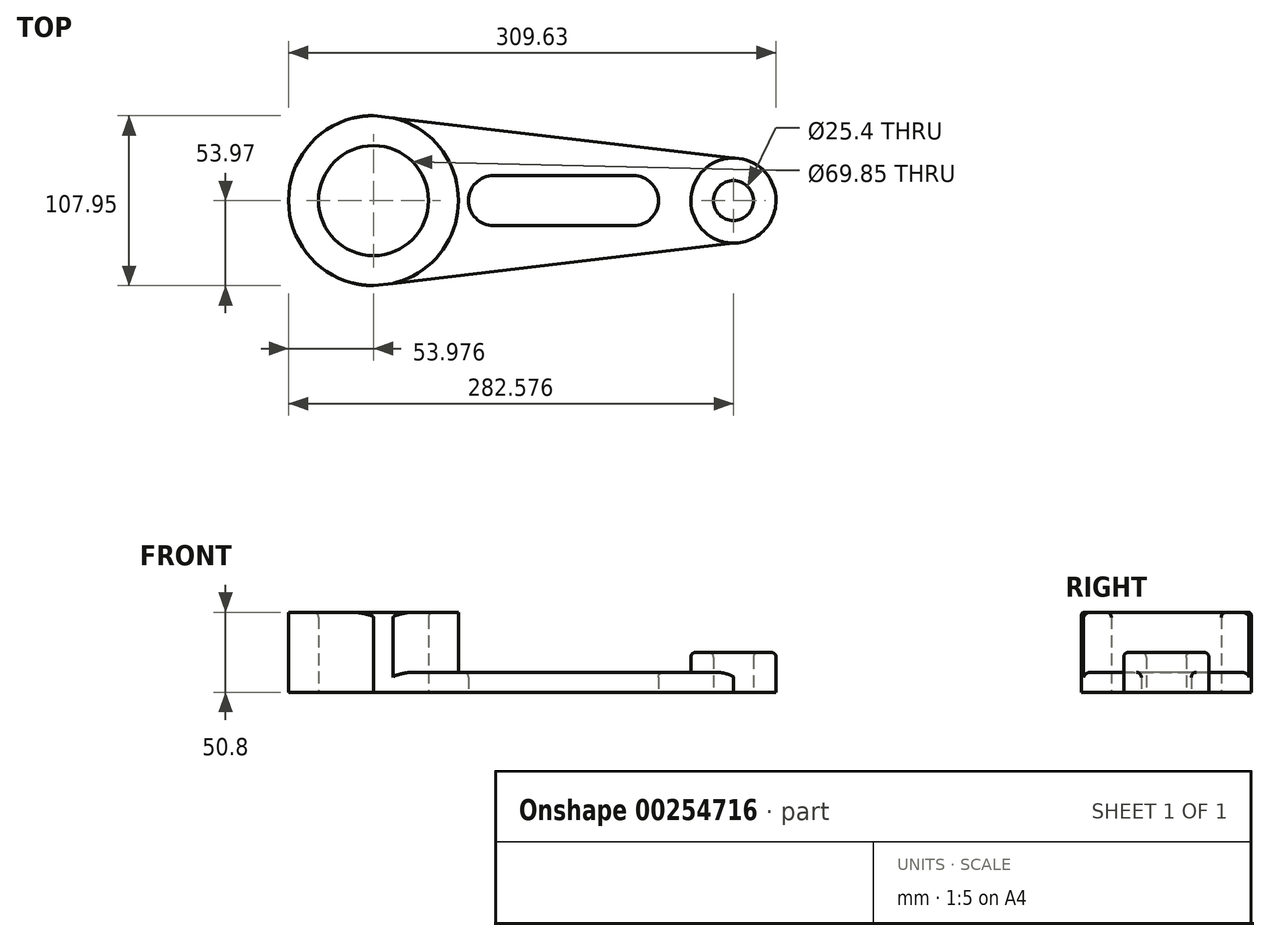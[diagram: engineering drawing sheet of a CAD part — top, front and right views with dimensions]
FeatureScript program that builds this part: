
annotation { "Feature Type Name" : "Feature", "Feature Type Description" : "" }
export const myFeature = defineFeature(function(context is Context, id is Id, definition is map)
    precondition{}
    {
        {
            var Q0;
            Q0=qCreatedBy(makeId("Top.planeOp"),FACE);
            var sketch = newSketch(context, id + "F0", { "sketchPlane" : qUnion([Q0])});
            skCircle(sketch, "E0", {"center": v(-200.57, 15.87) * mm, "radius": 34.93 * mm});
            skCircle(sketch, "E1", {"center": v(-200.57, 15.87) * mm, "radius": 53.98 * mm});
            skCircle(sketch, "E2", {"center": v(28.03, 15.87) * mm, "radius": 12.7 * mm});
            skCircle(sketch, "E3", {"center": v(28.03, 15.87) * mm, "radius": 27.05 * mm});
            skArc(sketch, "E4", {"start": v(-124.37, 31.75) * mm, "mid": v(-140.25, 15.87) * mm, "end": v(-124.37, 0) * mm});
            skArc(sketch, "E5", {"start": v(-35.47, 0) * mm, "mid": v(-19.6, 15.87) * mm, "end": v(-35.47, 31.75) * mm});
            skLineSegment(sketch, "E6", {"start": v(-124.37, 31.75) * mm, "end": v(-35.47, 31.75) * mm});
            skLineSegment(sketch, "E7", {"start": v(-124.37, 0) * mm, "end": v(-35.47, 0) * mm});
            skLineSegment(sketch, "E8", {"start": v(-200.57, 69.85) * mm, "end": v(28.03, 42.92) * mm});
            skLineSegment(sketch, "E9", {"start": v(-200.57, -38.1) * mm, "end": v(28.03, -11.18) * mm});
            skSolve(sketch);
        }
        {
            var Q0;
            Q0=makeQuery(id+"F0.imprint","IMPRINT",FACE,{"disambiguationData":[TD([[makeQuery(id+"F0.imprint","IMPRINT",EDGE,{"derivedFrom":sQuery(id+"F0.wireOp",EDGE,"E4")}),-1.0]])]});
            extrude(context, id + "F1", {"entities" : qUnion([Q0]), "depth" : 12.7 * mm});
        }
        {
            var Q0;
            Q0=makeQuery(id+"F1.opExtrude","CAP_EDGE",EDGE,{"disambiguationData":[OSD([sQuery(id+"F0.wireOp",EDGE,"E9")])],"isStart":false});
            var Q1;
            Q1=makeQuery(id+"F1.opExtrude","CAP_EDGE",EDGE,{"disambiguationData":[OSD([sQuery(id+"F0.wireOp",EDGE,"E8")])],"isStart":false});
            fillet(context, id + "F2", {"entities" : qUnion([Q0, Q1]), "radius" : 3.17 * mm, "tangentPropagation" : true, "allowEdgeOverflow" : false});
        }
        {
            var Q0;
            Q0=makeQuery(id+"F0.imprint","IMPRINT",FACE,{"disambiguationData":[TD([[makeQuery(id+"F0.imprint","IMPRINT",EDGE,{"derivedFrom":sQuery(id+"F0.wireOp",EDGE,"E2")}),-1.0]])]});
            extrude(context, id + "F3", {"entities" : qUnion([Q0]), "operationType" : NewBodyOperationType.ADD, "depth" : 25.4 * mm});
        }
        {
            var Q0;
            Q0=makeQuery(id+"F0.imprint","IMPRINT",FACE,{"disambiguationData":[TD([[makeQuery(id+"F0.imprint","IMPRINT",EDGE,{"derivedFrom":sQuery(id+"F0.wireOp",EDGE,"E0")}),-1.0]])]});
            extrude(context, id + "F4", {"entities" : qUnion([Q0]), "operationType" : NewBodyOperationType.ADD, "depth" : 50.8 * mm});
        }
        {
            var Q0;
            {var subQ0=sQuery(id+"F0.wireOp",EDGE,"E1");Q0=makeQuery(id+"F4.opExtrude","CAP_EDGE",EDGE,{"disambiguationData":[OSD([subQ0]),TDD([makeQuery(id+"F0.imprint","IMPRINT",EDGE,{"disambiguationData":[TD([[makeQuery(id+"F0.imprint","INTERSECT",VERTEX,{"disambiguationData":[OD(0.0)],"derivedFrom":[subQ0,sQuery(id+"F0.wireOp",EDGE,"E8")]}),-1.0]])],"derivedFrom":subQ0})])],"isStart":false});}
            var Q1;
            {var subQ0=sQuery(id+"F0.wireOp",EDGE,"E1");Q1=makeQuery(id+"F4.opExtrude","CAP_EDGE",EDGE,{"disambiguationData":[OSD([subQ0]),TDD([makeQuery(id+"F0.imprint","IMPRINT",EDGE,{"disambiguationData":[TD([[makeQuery(id+"F0.imprint","INTERSECT",VERTEX,{"disambiguationData":[OD(1.0)],"derivedFrom":[subQ0,sQuery(id+"F0.wireOp",EDGE,"E8")]}),1.0]])],"derivedFrom":subQ0})])],"isStart":false});}
            var Q2;
            Q2=makeQuery(id+"F4.opExtrude","CAP_EDGE",EDGE,{"disambiguationData":[OSD([sQuery(id+"F0.wireOp",EDGE,"E9")])],"isStart":false});
            var Q3;
            Q3=makeQuery(id+"F4.opExtrude","CAP_EDGE",EDGE,{"disambiguationData":[OSD([sQuery(id+"F0.wireOp",EDGE,"E8")])],"isStart":false});
            var Q4;
            Q4=makeQuery(id+"F3.opExtrude","CAP_EDGE",EDGE,{"disambiguationData":[OSD([sQuery(id+"F0.wireOp",EDGE,"E3")])],"isStart":false});
            fillet(context, id + "F5", {"entities" : qUnion([Q0, Q1, Q2, Q3, Q4]), "radius" : 3.17 * mm, "tangentPropagation" : true, "allowEdgeOverflow" : false});
        }
        {
            var Q0;
            Q0=makeQuery(id+"F4.opExtrude","CAP_EDGE",EDGE,{"disambiguationData":[OSD([sQuery(id+"F0.wireOp",EDGE,"E0")])],"isStart":false});
            var Q1;
            Q1=makeQuery(id+"F3.opExtrude","CAP_EDGE",EDGE,{"disambiguationData":[OSD([sQuery(id+"F0.wireOp",EDGE,"E2")])],"isStart":false});
            var Q2;
            Q2=makeQuery(id+"F1.opExtrude","CAP_EDGE",EDGE,{"disambiguationData":[OSD([sQuery(id+"F0.wireOp",EDGE,"E7")])],"isStart":false});
            var Q3;
            Q3=makeQuery(id+"F1.opExtrude","CAP_EDGE",EDGE,{"disambiguationData":[OSD([sQuery(id+"F0.wireOp",EDGE,"E4")])],"isStart":false});
            var Q4;
            Q4=makeQuery(id+"F1.opExtrude","CAP_EDGE",EDGE,{"disambiguationData":[OSD([sQuery(id+"F0.wireOp",EDGE,"E5")])],"isStart":false});
            var Q5;
            Q5=makeQuery(id+"F1.opExtrude","CAP_EDGE",EDGE,{"disambiguationData":[OSD([sQuery(id+"F0.wireOp",EDGE,"E6")])],"isStart":false});
            fillet(context, id + "F6", {"entities" : qUnion([Q0, Q1, Q2, Q3, Q4, Q5]), "radius" : 3.17 * mm, "tangentPropagation" : true, "allowEdgeOverflow" : false});
        }
    });
